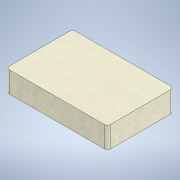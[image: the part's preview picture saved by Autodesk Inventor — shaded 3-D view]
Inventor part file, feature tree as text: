
AUTODESK INVENTOR PART (.ipt)
format: ipt  version: 2021 (Build 250183000, 183)  size: 112,640 bytes
history: native  units: mm
features: extrude x1, sketch x1
ambient origin geometry x8: Origin, YZ Plane, XZ Plane, XY Plane, X Axis, Y Axis, Z Axis, Center Point
bodies: Solid1 (feature_tree)
feature tree (2):
  extrude  "Extrusion1"  Depth=42.0mm
  sketch  "Sketch1"  dims[d0=64.0mm d1=42.0mm d2=2.0mm d3=13.35mm d4=0.0mm]
